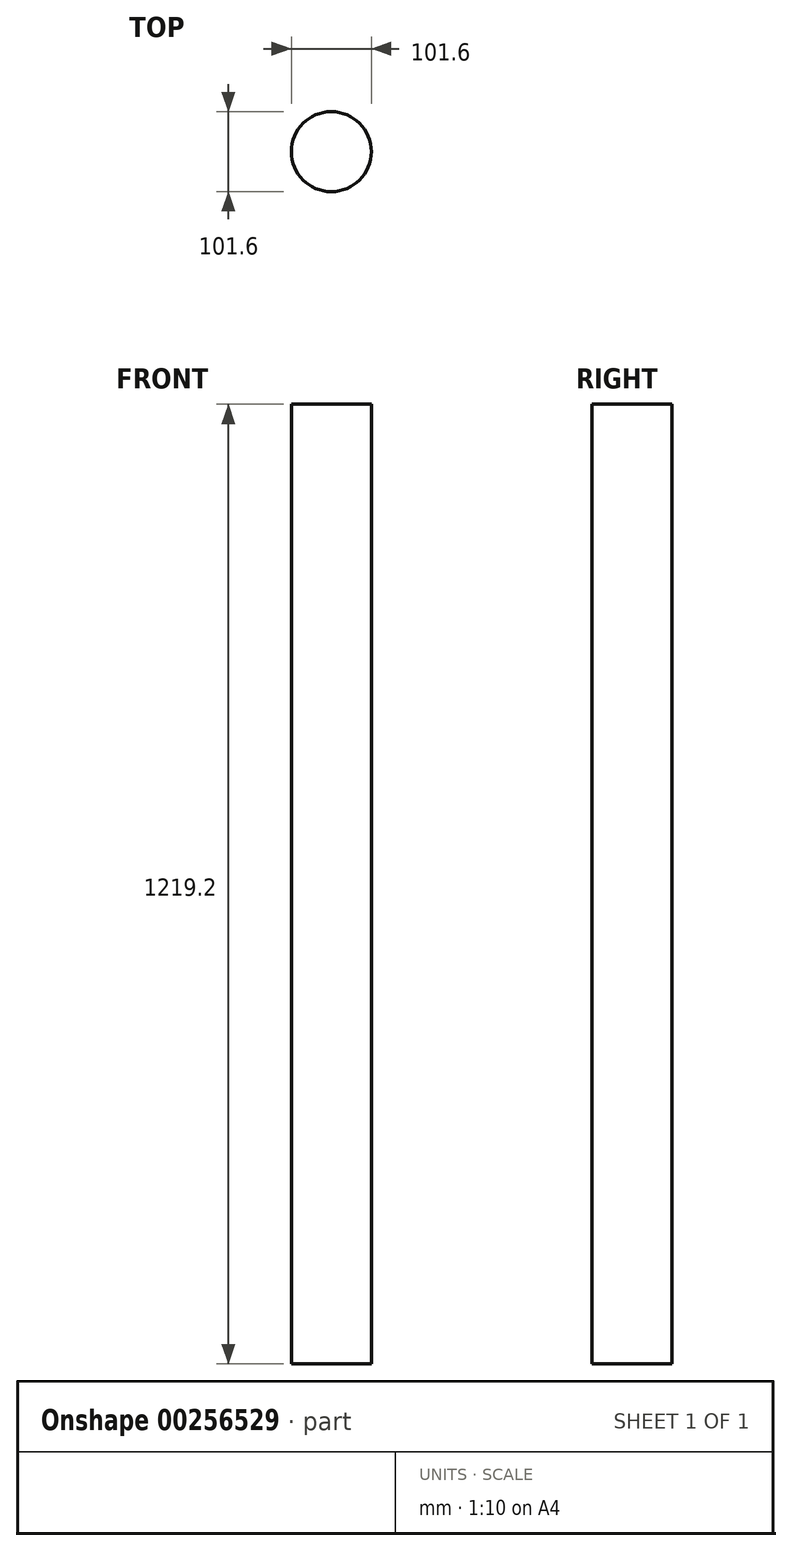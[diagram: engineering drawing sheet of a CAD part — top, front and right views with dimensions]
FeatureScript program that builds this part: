
annotation { "Feature Type Name" : "Feature", "Feature Type Description" : "" }
export const myFeature = defineFeature(function(context is Context, id is Id, definition is map)
    precondition{}
    {
        {
            var Q0;
            Q0=qCreatedBy(makeId("Top.planeOp"),FACE);
            var sketch = newSketch(context, id + "F0", { "sketchPlane" : qUnion([Q0])});
            skCircle(sketch, "E0", {"center": v(0, 0) * mm, "radius": 50.8 * mm});
            skSolve(sketch);
        }
        {
            var Q0;
            Q0 = qSketchRegion(id + "F0", true);
            extrude(context, id + "F1", {"entities" : qUnion([Q0]), "depth" : 1219.2 * mm});
        }
    });
